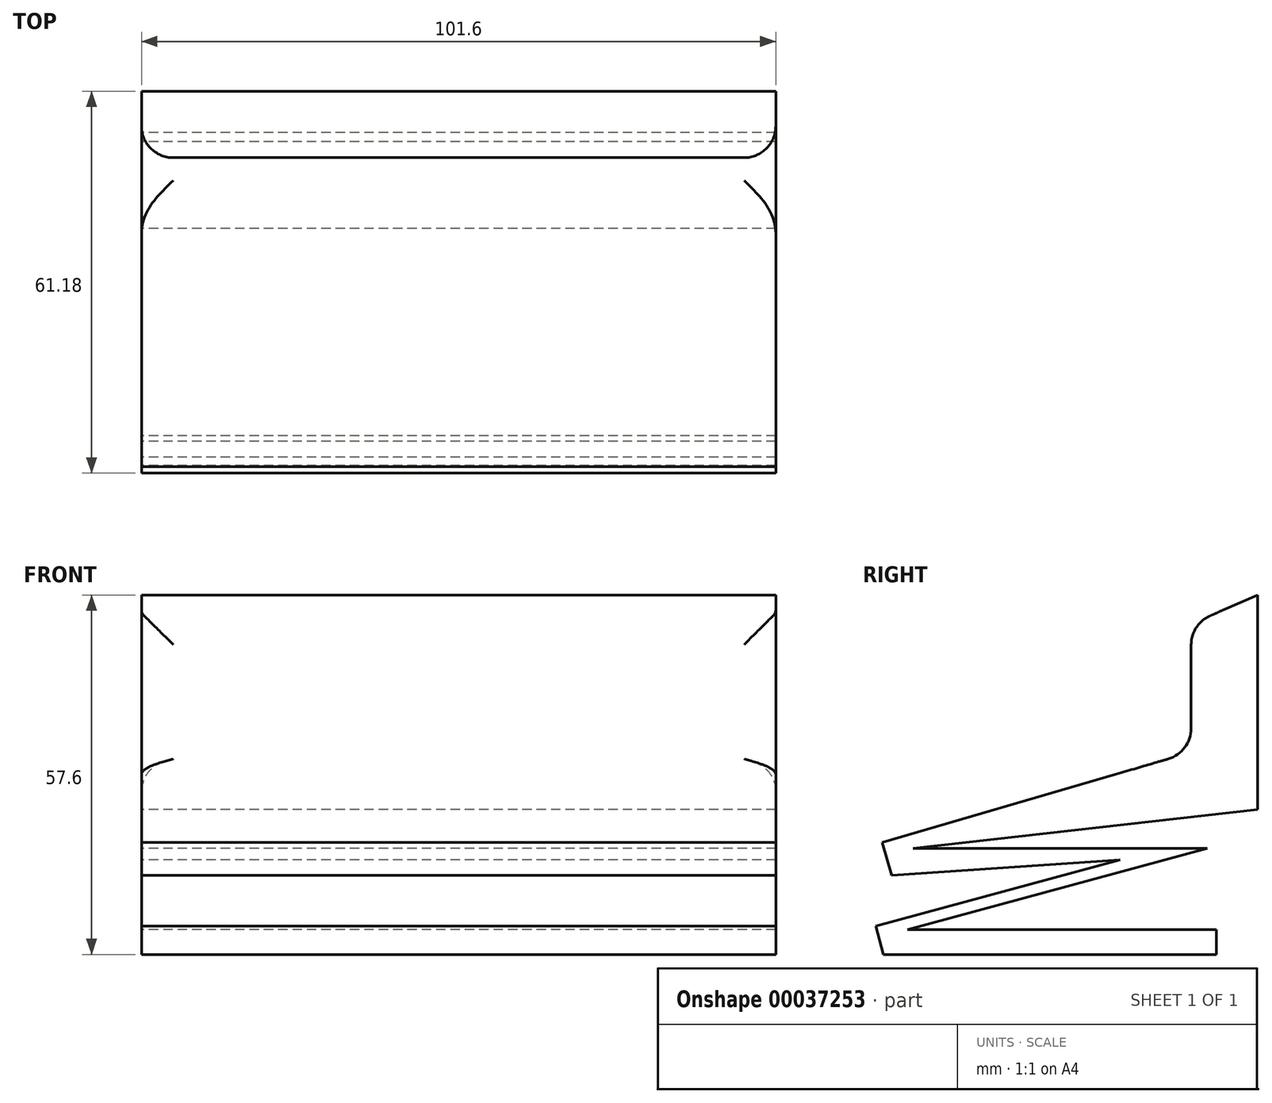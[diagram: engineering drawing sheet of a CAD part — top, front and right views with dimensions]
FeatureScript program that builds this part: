
annotation { "Feature Type Name" : "Feature", "Feature Type Description" : "" }
export const myFeature = defineFeature(function(context is Context, id is Id, definition is map)
    precondition{}
    {
        {
            var Q0;
            Q0=qCreatedBy(makeId("Right.planeOp"),FACE);
            var sketch = newSketch(context, id + "F0", { "sketchPlane" : qUnion([Q0])});
            skLineSegment(sketch, "E0", {"start": v(15.4, -53.61) * mm, "end": v(-34.1, -53.61) * mm});
            skLineSegment(sketch, "E1", {"start": v(-34.1, -53.61) * mm, "end": v(13.93, -40.6) * mm});
            skLineSegment(sketch, "E2", {"start": v(13.93, -40.6) * mm, "end": v(-33.18, -40.6) * mm});
            skLineSegment(sketch, "E3", {"start": v(-33.18, -40.6) * mm, "end": v(22, -34.37) * mm});
            skLineSegment(sketch, "E4", {"start": v(22, -34.37) * mm, "end": v(22, 0) * mm});
            skLineSegment(sketch, "E5", {"start": v(22, 0) * mm, "end": v(11.36, -4.67) * mm});
            skLineSegment(sketch, "E6", {"start": v(11.36, -4.67) * mm, "end": v(11.36, -25.2) * mm});
            skLineSegment(sketch, "E7", {"start": v(11.36, -25.2) * mm, "end": v(-38.13, -39.68) * mm});
            skLineSegment(sketch, "E8", {"start": v(-38.13, -39.68) * mm, "end": v(-36.6, -44.9) * mm});
            skLineSegment(sketch, "E9", {"start": v(-36.6, -44.9) * mm, "end": v(0, -42.43) * mm});
            skLineSegment(sketch, "E10", {"start": v(0, -42.43) * mm, "end": v(-39.18, -53.05) * mm});
            skLineSegment(sketch, "E11", {"start": v(-39.18, -53.05) * mm, "end": v(-37.95, -57.6) * mm});
            skLineSegment(sketch, "E12", {"start": v(-37.95, -57.6) * mm, "end": v(15.4, -57.6) * mm});
            skLineSegment(sketch, "E13", {"start": v(15.4, -57.6) * mm, "end": v(15.4, -53.61) * mm});
            skSolve(sketch);
        }
        {
            var Q0;
            Q0=makeQuery(id+"F0.imprint","IMPRINT",FACE,{"disambiguationData":[TD([[makeQuery(id+"F0.imprint","IMPRINT",EDGE,{"derivedFrom":sQuery(id+"F0.wireOp",EDGE,"E0")}),1.0]])]});
            extrude(context, id + "F1", {"entities" : qUnion([Q0]), "depth" : 101.6 * mm});
        }
        {
            var Q0;
            Q0=makeQuery(id+"F1.opExtrude","SWEPT_FACE",FACE,{"disambiguationData":[OSD([sQuery(id+"F0.wireOp",EDGE,"E6")])]});
            fillet(context, id + "F2", {"entities" : qUnion([Q0]), "radius" : 5.08 * mm, "tangentPropagation" : true, "allowEdgeOverflow" : false});
        }
    });
